# Revit family: Mirror-45cm60cm80cm100cm120cm-IlluminatedMirror-Vitra-İntegraSeries-61305+61306+61307+61308+61309
name_source: partatom
category: Furniture Systems
revit_build: Autodesk Revit 2017 (Build: 20160225_1515(x64)
units: mm (PartAtom-declared; Revit-internal decimal feet)

## family parameters
Cut with Voids When Loaded = No
Host = Face
OmniClass Number = 23.40.00.00
OmniClass Title = Equipment and Furnishings
Part Type = Normal
Room Calculation Point = No
Round Connector Dimension = Use Diameter
Shared = Yes

## types (5) — shared parameters
BIMobject category = Sanitary - Mirrors
Construction Type = Wall Mounted
Depth(mm) = 40 mm
Description = İntegra Illuminated Mirror
Design country = Turkey
Height(mm) = 700 mm  [stored 2.29659 ft]
IFC Classification = Furnishing Element
Lighting Type = Ambiance Led Lighting
Manufacturer = Vitra
Manufacturer name = Vitra
Masterformat 2014 Code = 12 50 00
Masterformat 2014 Description = Furniture
NBS Referans Code = 45-55-06
NBS Referans Description = Bathroom Mirrors
Nominal height = 0.000
Nominal width = 0.000
OmniClass Code = 23-21 37 13 15
OmniClass Description = Mirrors
Primary Material = Mirror
Product certification = https://www.vitraglobal.com
Product data url = https://www.vitra-bad.fr
Product family = İntegra
Product group = Bathroom Furniture
Technical description = http://cdn.vitra.com.tr
UNSPSC Code = 56
UNSPSC Description = Furniture and Furnishings
URL = https://vitraglobal.com
Uniclass 1.4 Code = L8732
Uniclass 1.4 Description = Mirrors
Uniclass 2.0 Code = PR-45-55-06
Uniclass 2.0 Description = Bathroom Mirrors
Uniclass 2015 Code = Pr_25_71_53_06
Uniclass 2015 Name = Bathroom mirrors
Uniformat II Code = E2010
Uniformat II Description = Furnishings
Voltage = 220V
Warranty Period (Year) = 2
Youtube = https://www.youtube.com
zero-valued in all types: Default Elevation

## per-type parameters (varying)
| type | Article No. (default) | Model | Product SKU | Weight Net (kg) | Width(mm) |
| Mirror-45cm-IlluminatedMirror-Vitra-İntegraSeries-61305 | 61305 | 61305 | 61305 | 7 | 450 mm  [stored 1.47638 ft] |
| Mirror-60cm-IlluminatedMirror-Vitra-İntegraSeries-61306 | 61306 | 61309 | 61306 | 9 | 600 mm |
| Mirror-80cm-IlluminatedMirror-Vitra-İntegraSeries-61307 | 61307 | 61307 | 61307 | 11 | 800 mm  [stored 2.62467 ft] |
| Mirror-100cm-IlluminatedMirror-Vitra-İntegraSeries-61308 | 61308 | 61308 | 61308 | 13 | 1000 mm  [stored 3.28084 ft] |
| Mirror-120cm-IlluminatedMirror-Vitra-İntegraSeries-61309 | 61309 | 61309 | 61309 | 15 | 1200 mm |

note: [stored X ft] marks values corroborated as IEEE doubles in the binary element streams (Revit-internal decimal feet)

## geometry (parser evidence)
native form markers: Sweep x3
no freeform markers — native parametric forms only
